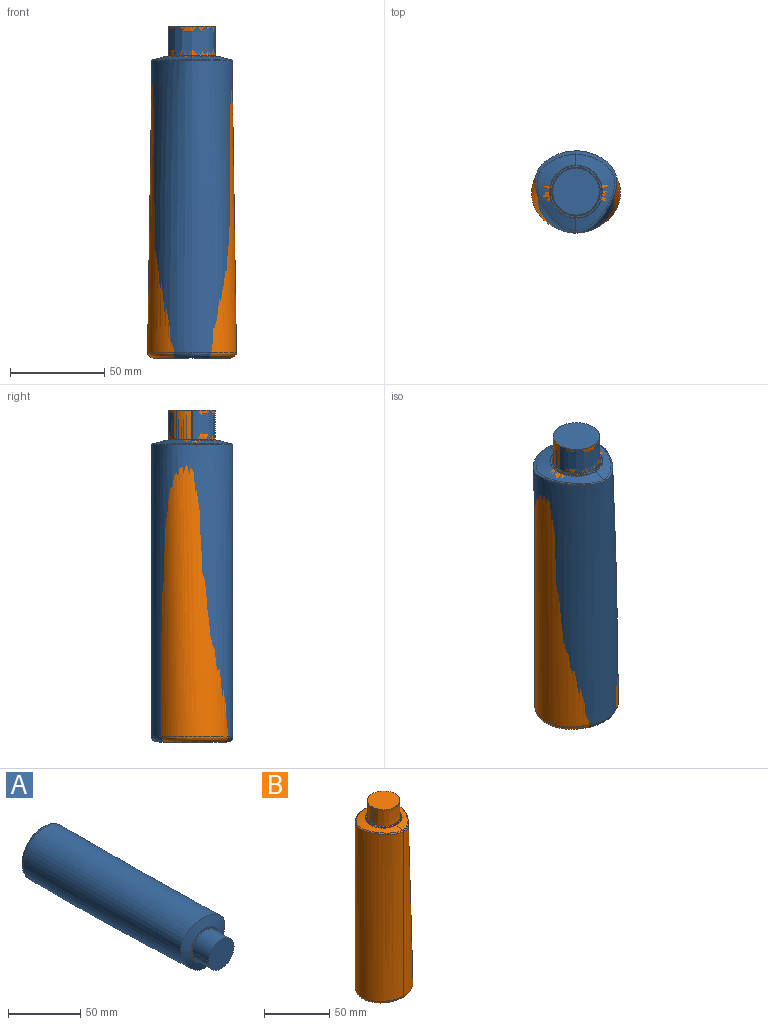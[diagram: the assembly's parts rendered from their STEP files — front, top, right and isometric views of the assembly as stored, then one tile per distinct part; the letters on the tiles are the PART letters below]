
ASSEMBLY  parts=2 mates=1
PART A: 11 faces, bbox 43.3x175.8x43.3 mm
  f0: plane 37.28x37.28mm, normal (0,1,0), area 1090.7mm2, adj f1,f2
  f1: bspline ~43.27x21.65mm, area 304.1mm2, adj f0,f2,f4
  f2: bspline ~43.27x21.62mm, area 304mm2, adj f0,f1,f4
  f3: plane 24.78x24.78mm, normal (0,-1,0), area 481.9mm2, adj f5,f6
  f4: bspline ~154.73x43.27mm, area 20911.4mm2, adj f1,f2,f7
  f5: cylinder r=12.39mm len=24.77mm, axis (0,-1,0), area 605.7mm2, adj f3,f6,f8,f9
  f6: extruded ~24.77x15.57mm, area 605.7mm2, adj f3,f5,f9
  f7: bspline ~43.24x43.24mm, area 830.4mm2, adj f4,f10
  f8: revolved ~21.97x12.88mm, area 23.2mm2, adj f5,f9,f10
  f9: bspline ~25.85x22.04mm, area 38.8mm2, adj f5,f6,f8,f10
  f10: plane 27.82x27.78mm, normal (0,-1,0), area 84.1mm2, adj f7,f8,f9
PART B: 19 faces, bbox 47.2x41.7x175.8 mm
  f0: plane 24.77x24.77mm, normal (0,0,1), area 481.9mm2, adj f11,f18
  f1: bspline ~35.68x20.54mm, area 244.3mm2, adj f2,f10,f12
  f2: plane 32.86x28.54mm, normal (0,0,-1), area 736mm2, adj f1,f12
  f3: bspline ~25.77x22.01mm, area 38.8mm2, adj f4,f7,f11,f18
  f4: revolved ~21.97x12.88mm, area 23.2mm2, adj f3,f7,f11
  f5: bspline ~28.05x14.75mm, area 13.2mm2, adj f6,f7,f13,f14
  f6: bspline ~41.68x21.21mm, area 328.4mm2, adj f5,f14,f15
  f7: plane 27.5x27.49mm, normal (0,0,1), area 70.2mm2, adj f3,f4,f5,f13
  f8: bspline ~41.67x21.22mm, area 80.3mm2, adj f14,f15,f16
  f9: bspline ~157.73x41.68mm, area 10369.5mm2, adj f10,f15,f16
  f10: bspline ~41.67x24.08mm, area 317.2mm2, adj f1,f9,f12,f16,f17
  f11: cylinder r=12.39mm len=24.77mm, axis (0,0,1), area 605.7mm2, adj f0,f3,f4,f18
  f12: bspline ~35.68x20.53mm, area 244.3mm2, adj f1,f2,f10,f17
  f13: bspline ~28x14.01mm, area 12.9mm2, adj f5,f7,f14
  f14: bspline ~40.37x20.49mm, area 328.3mm2, adj f5,f6,f8,f13,f15
  f15: bspline ~41.67x21.7mm, area 81.6mm2, adj f6,f8,f9,f14,f16
  f16: bspline ~154.08x41.68mm, area 10476.7mm2, adj f8,f9,f10,f15,f17
  f17: bspline ~41.68x23.64mm, area 312.2mm2, adj f10,f12,f16
  f18: extruded ~24.77x15.57mm, area 605.7mm2, adj f0,f3,f11
PLACE A rot(axis=(-1,0,0),90deg) t=(-1158.87,0.37,0)mm
PLACE B at identity
MATE fastened A.f5 <-> B.f11  axis (0,0,1) through (0,0,175.8)mm
